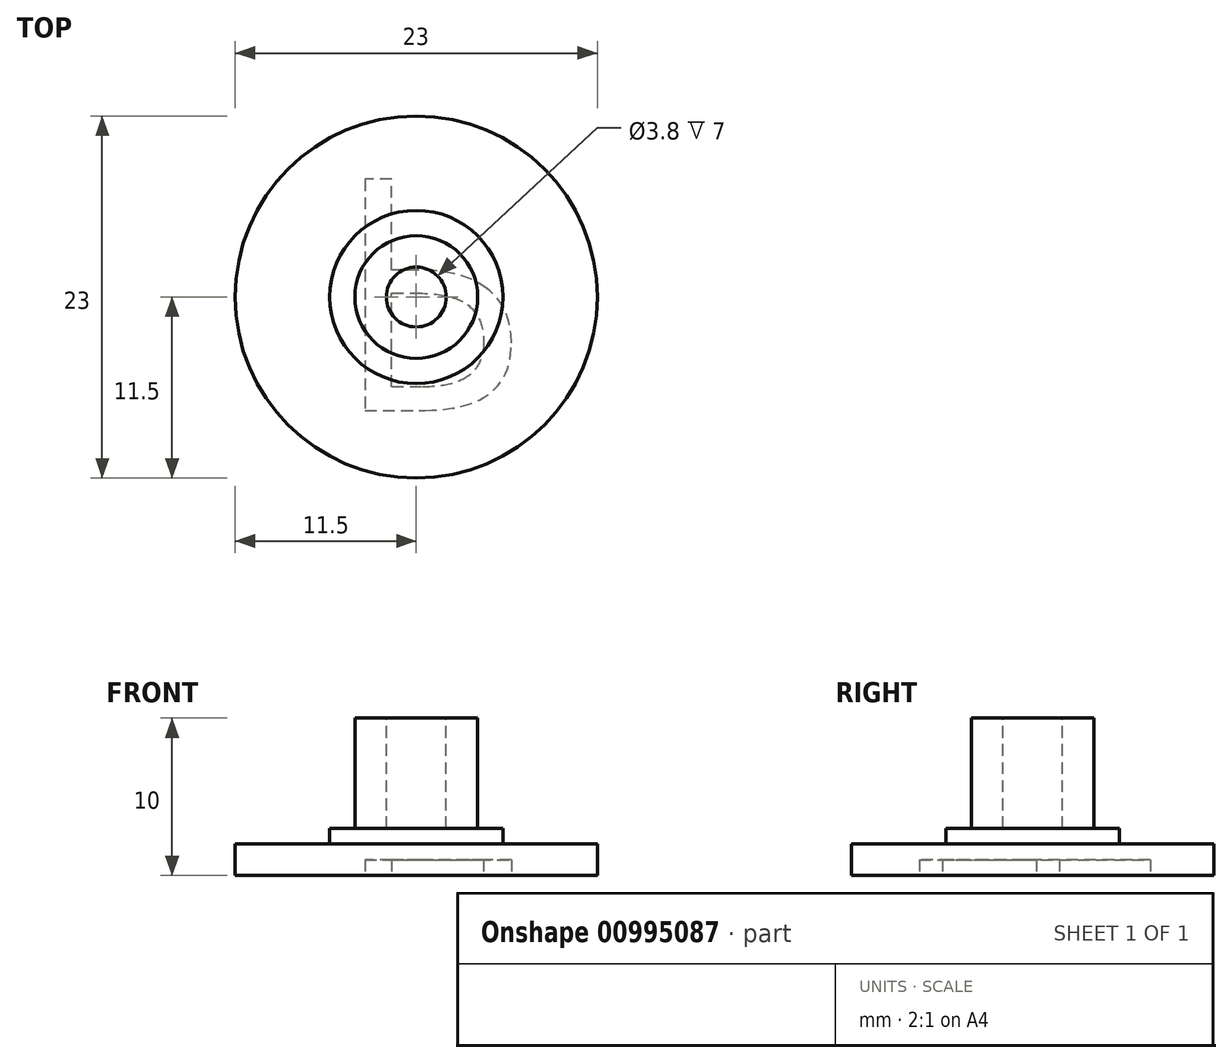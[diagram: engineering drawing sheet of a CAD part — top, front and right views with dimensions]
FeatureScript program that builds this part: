
annotation { "Feature Type Name" : "Feature", "Feature Type Description" : "" }
export const myFeature = defineFeature(function(context is Context, id is Id, definition is map)
    precondition{}
    {
        {
            var Q0;
            Q0=qCreatedBy(makeId("Top.planeOp"),FACE);
            var sketch = newSketch(context, id + "F0", { "sketchPlane" : qUnion([Q0])});
            skCircle(sketch, "E0", {"center": v(0, 0) * mm, "radius": 11.5 * mm});
            skSolve(sketch);
        }
        {
            var Q0;
            Q0=makeQuery(id+"F0.imprint","IMPRINT",FACE,{"disambiguationData":[TD([[makeQuery(id+"F0.imprint","IMPRINT",EDGE,{"derivedFrom":sQuery(id+"F0.wireOp",EDGE,"E0")}),1.0]])]});
            extrude(context, id + "F1", {"entities" : qUnion([Q0]), "depth" : 2 * mm, "offsetDistance" : 25 * mm});
        }
        {
            var Q0;
            Q0=makeQuery(id+"F1.opExtrude","CAP_FACE",FACE,{"disambiguationData":[OSD([sQuery(id+"F0.wireOp",EDGE,"E0")])],"isStart":false});
            var sketch = newSketch(context, id + "F2", { "sketchPlane" : qUnion([Q0])});
            skCircle(sketch, "E1", {"center": v(0, 0) * mm, "radius": 5.5 * mm});
            skSolve(sketch);
        }
        {
            var Q0;
            Q0=makeQuery(id+"F2.imprint","IMPRINT",FACE,{"disambiguationData":[TD([[makeQuery(id+"F2.imprint","IMPRINT",EDGE,{"derivedFrom":sQuery(id+"F2.wireOp",EDGE,"E1")}),1.0]])]});
            extrude(context, id + "F3", {"entities" : qUnion([Q0]), "operationType" : NewBodyOperationType.ADD, "depth" : 1 * mm, "offsetDistance" : 25 * mm});
        }
        {
            var Q0;
            Q0=makeQuery(id+"F3.opExtrude","CAP_FACE",FACE,{"disambiguationData":[OSD([sQuery(id+"F2.wireOp",EDGE,"E1")])],"isStart":false});
            var sketch = newSketch(context, id + "F4", { "sketchPlane" : qUnion([Q0])});
            skCircle(sketch, "E2", {"center": v(0, 0) * mm, "radius": 3.9 * mm});
            skSolve(sketch);
        }
        {
            var Q0;
            Q0 = qSketchRegion(id + "F4", true);
            extrude(context, id + "F5", {"entities" : qUnion([Q0]), "operationType" : NewBodyOperationType.ADD, "depth" : 7 * mm, "offsetDistance" : 25 * mm});
        }
        {
            var Q0;
            Q0=makeQuery(id+"F5.opExtrude","CAP_FACE",FACE,{"disambiguationData":[OSD([sQuery(id+"F4.wireOp",EDGE,"E2")])],"isStart":false});
            var sketch = newSketch(context, id + "F6", { "sketchPlane" : qUnion([Q0])});
            skCircle(sketch, "E3", {"center": v(0, 0) * mm, "radius": 1.9 * mm});
            skSolve(sketch);
        }
        {
            var Q0;
            Q0=makeQuery(id+"F6.imprint","IMPRINT",FACE,{"disambiguationData":[TD([[makeQuery(id+"F6.imprint","IMPRINT",EDGE,{"derivedFrom":sQuery(id+"F6.wireOp",EDGE,"E3")}),1.0]])]});
            extrude(context, id + "F7", {"entities" : qUnion([Q0]), "operationType" : NewBodyOperationType.REMOVE, "oppositeDirection" : true, "depth" : 7 * mm, "offsetDistance" : 25 * mm});
        }
        {
            var Q0;
            Q0=makeQuery(id+"F1.opExtrude","CAP_FACE",FACE,{"disambiguationData":[OSD([sQuery(id+"F0.wireOp",EDGE,"E0")])],"isStart":true});
            var sketch = newSketch(context, id + "F8", { "sketchPlane" : qUnion([Q0])});
            skText(sketch, "E4", { "text": "P", "fontName": "OpenSans-Regular.ttf"});
            const initialGuessF8  = {"E4": [-0.00528, -0.00748, 1, 0, 0.0148]};
            skSetInitialGuess(sketch, initialGuessF8);
            skSolve(sketch);
        }
        {
            var Q0;
            Q0 = qSketchRegion(id + "F8", true);
            extrude(context, id + "F9", {"entities" : qUnion([Q0]), "operationType" : NewBodyOperationType.REMOVE, "oppositeDirection" : true, "depth" : 1 * mm, "offsetDistance" : 25 * mm});
        }
    });
